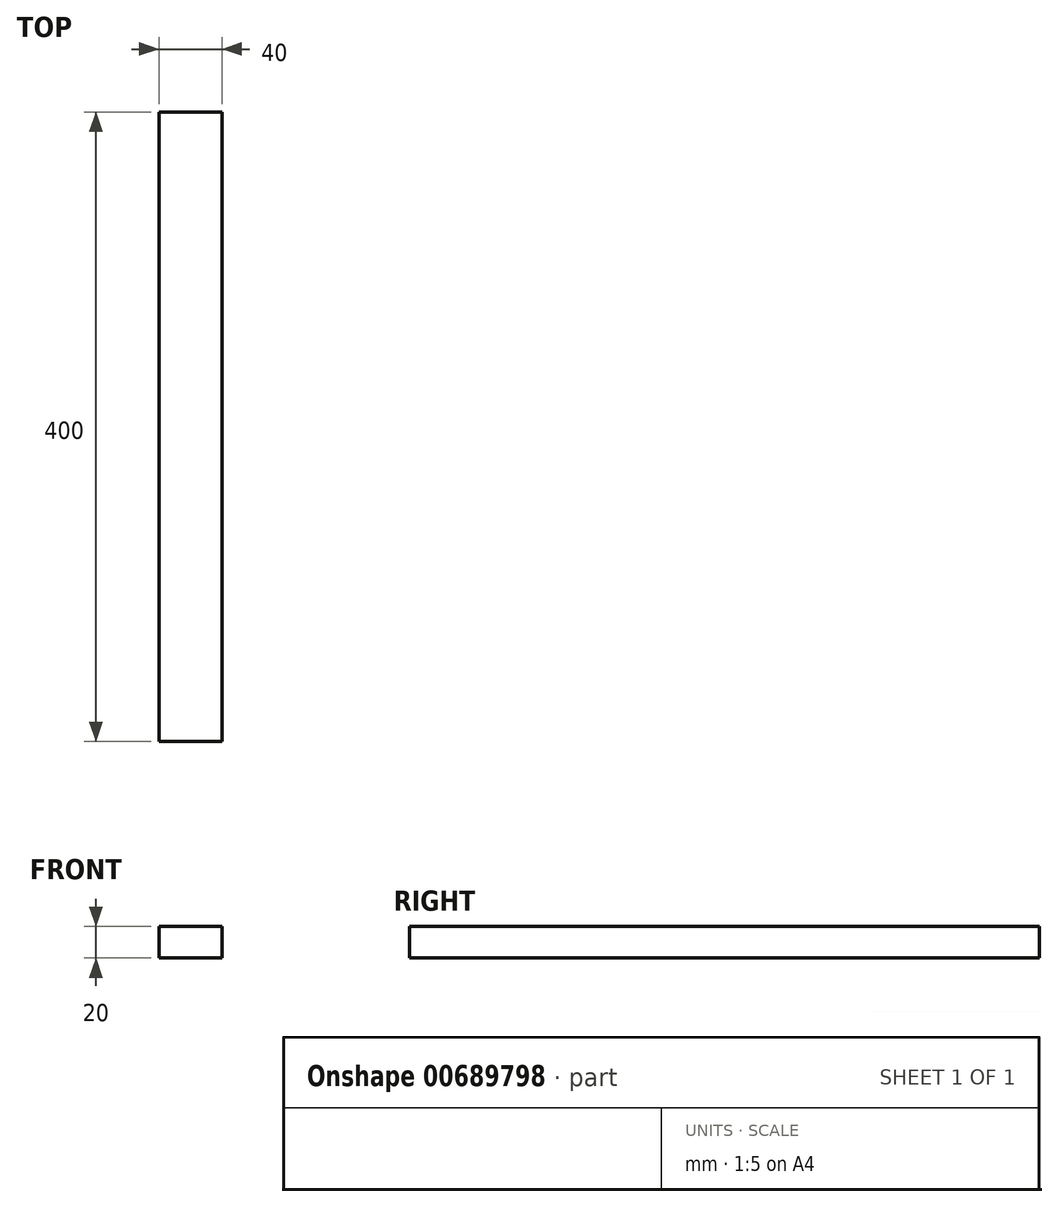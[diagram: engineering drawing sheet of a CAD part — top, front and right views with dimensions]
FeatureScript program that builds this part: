
annotation { "Feature Type Name" : "Feature", "Feature Type Description" : "" }
export const myFeature = defineFeature(function(context is Context, id is Id, definition is map)
    precondition{}
    {
        {
            var Q0;
            Q0=qCreatedBy(makeId("Front.planeOp"),FACE);
            var sketch = newSketch(context, id + "F0", { "sketchPlane" : qUnion([Q0])});
            skLineSegment(sketch, "E0.bottom", {"start": v(0, 0) * mm, "end": v(40, 0) * mm});
            skLineSegment(sketch, "E0.top", {"start": v(0, 20) * mm, "end": v(40, 20) * mm});
            skLineSegment(sketch, "E0.left", {"start": v(0, 0) * mm, "end": v(0, 20) * mm});
            skLineSegment(sketch, "E0.right", {"start": v(40, 0) * mm, "end": v(40, 20) * mm});
            skSolve(sketch);
        }
        {
            var Q0;
            Q0=makeQuery(id+"F0.imprint","IMPRINT",FACE,{"disambiguationData":[TD([[makeQuery(id+"F0.imprint","IMPRINT",EDGE,{"derivedFrom":sQuery(id+"F0.wireOp",EDGE,"E0.bottom")}),1.0]])]});
            extrude(context, id + "F1", {"entities" : qUnion([Q0]), "depth" : 400 * mm, "offsetDistance" : 25 * mm});
        }
    });
